# Revit family: Electronics_Wall-Stations_Biamp_Vocia_Emergency-Wall-Paging-Station_EWS-4_10__
name_source: partatom
category: Communication Devices
units: mm (PartAtom-declared; Revit-internal decimal feet)

## family parameters
Cut with Voids When Loaded = No
Host = Face
Maintain Annotation Orientation = No
OmniClass Number = 23.85.10.11.14
OmniClass Title = Audio Equipment
Part Type = Normal
Room Calculation Point = No
Round Connector Dimension = Use Diameter
Shared = No

## types (2) — shared parameters
12V DC Out = 50mA
A/D Converters = 24-bit
Altitude = 0-10,000 ft (0-3000m) MSL
Apparent Load = 0 VA
Balanced Line In = -10dB Nominal
Compliance = EN 54-16 certified CE marked (Europe) RCM (Australia) EAC (Eurasian Customs Union) RINA (Italy) RoHS Directive (Europe) EN 60849, AS 60849 verified
Connector Description = PoE 802.3af Class 2
Default Elevation = 4' - 0"
Depth = 0' - 1 29/32"
Effective Input Headroom = 30dB
Frequency Response = 100Hz ~ 20kHz: +0, -1dB
Gain = Adjustable in 1dB steps over a 30dB range
Height = 0' - 5 5/16"
Housing Material = Biamp - Plastic - Black
Humidity = 0-95% relative humidity (non-condensing)
Input Impedance = 3 kohm
Manufacturer = Biamp
Max Power Consumption = 0 W
Maximum Input = 125dB SPL
Microphone Cord Length = 4' - 0"
Microphone Frequency Response = 100Hz-10kHz
Microphone Pattern = Cardioid
Microphone Type = Noise cancelling dynamic microphone with dual transducer (monitored)
Network Connection = RJ-45 with shielded Ethernet (CAT5, CAT5e, CAT6 or CAT7
Number of Poles = 1
PTT = Switch contact between pin and ground
Power Factor = 1
Product Documentation Link = https://downloads.biamp.com
Product Page URL = https://www.biamp.com
Product data url = https://www.bimobject.com
RS-232 = 57600 kbps
Sample Rate = 48kHz
System Headroom = 18dB
THD+N = 100Hz ~ 8kHz: <0.05%
Temperature Range = 23 - 104° F (-5 – 40° C)
URL = https://www.biamp.com
Voltage = 0 V
Weight = 2.60 lbf
Width = 0' - 11 29/32"

## per-type parameters (varying)
| type | Description | EWS-10 | EWS-4 | Model |
| EWS-4 | Vocia® EWS-4 Emergency Wall Paging Station | No | Yes | Vocia EWS-4 |
| EWS-10 | Vocia® EWS-10 Emergency Wall Paging Station | Yes | No | Vocia EWS-10 |

## geometry (parser evidence)
native form markers: Sweep x5
no freeform markers — native parametric forms only
